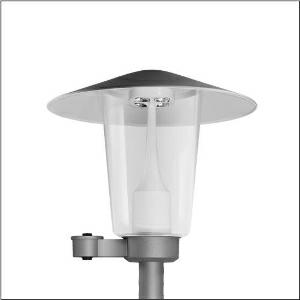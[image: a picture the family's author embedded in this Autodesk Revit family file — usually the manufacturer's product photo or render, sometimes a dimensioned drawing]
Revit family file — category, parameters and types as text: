
# Revit family: pilzleuchte_iq___st1_2a_5xa5235eu14h000022_6897
name_source: partatom
category: Lighting Fixtures
units: mm (PartAtom-declared; Revit-internal decimal feet)

## family parameters
Cut with Voids When Loaded = No
Host = Face
Light Source = No
Part Type = Normal
Room Calculation Point = No
Round Connector Dimension = Use Diameter
Shared = No

## types (1)
- --- (1 x LED, 1550 lm, 10.7 W, 3000K)
    Apparent Load = 11 VA
    CIE Flux Codes = 24 61 93 98 100
    Color Rendering = 70
    Color Temperature = 3000K
    Default Elevation = 1800 mm
    Description = Mushroom Luminaire iQ, mast luminaire, Module 540 iQ-SR, primary light control with 3 zone facetted reflector, of plastic, silver coated, highly specular, structured, primary optical cover: cover, of PMMA, transparent, light distribution: ST1.2a, light emission: direct distribution, primary light characteristic: asymmetric, installation type: post-top, LED, High Power LED, rated luminous flux: 1.550lm, luminous efficacy: 145lm/W, light colour: 730, colour temperature: 3000K, control gear: iQ-Street Remote, D4i with power reduction, control: optimised constant luminous flux control (CLO 2.0), Desk-Remote (wireless, voltage-free reading and setting of iQ features in the workshop via application-optimized NFC function/RFID function), Light-Fading, Smart-Wire, Night-Set, Lumen-Switch, Temp-Guard, Auto-Match, Street-Remote, pre-setting: logarithmic dimming characteristic, with terminal, 6-pole, max. 2.5mm², mains connection: 230..240V, AC, 50/60Hz, connection cable pre-assembled, cable length: 5,5m, wiring characteristics: H07RN-F, start of lifetime: 11W, end of service life: 11W, reduction: 6W, luminaire housing, upper part, of glass-fibre reinforced polyester, coated, Siteco® metallic grey (DB 702S), diameter: 650mm, height: 586mm, spigot size: d x l = 76 x 70mm (post-top) | with reducer (optional accessory) 60 x 70mm, mounting height: 3..5m, post-top mast mounting element, of diecast aluminium, coated, Siteco® metallic grey (DB 702S), Module 540 iQ-SR, traffic white (RAL 9016), equipment: standard, Smart Interface below, protection rating (complete): IP65, insulation class (complete): insulation class II (safety insulation), certification: CE, ENEC, VDE, packaging unit: 1 piece

Light Distribution: ST1.2a
    Height = 586 mm
    Lamp = 1 x LED
    Lamp Light Flux = 1550 lm
    Lamp Power = 10.7 W
    Lamp count = 1
    Length = 650 mm
    Luminous efficacy = 145 lm/W
    Manufacturer = Siteco
    ModVariant = No
    Model = 5XA5235EU14H000022
    Number of Poles = 1
    OnlyDefault = Yes
    Power Factor = 1
    Product Name = Pilzleuchte iQ | ST1.2a
    Product group = mast luminaire | pylon top
    ProductGroupID = 6100
    Protection Class = Protection class II
    Protection Degree = IP 65
    RLX_Detail_Level = 1
    RLX_Emergency_Light_Flux = 0 lm
    RLX_Emergency_Type = 0
    RLX_Emergency_Type_DB = No
    RlxData = <blob elided: 51765 chars, md5=b7cebe9e>
    Socket = socket
    Standby Power = 0 W
    System Light Flux = 1550 lm
    System Power = 11 W
    Type Comments = factory setting: luminous flux: 100 % | dim-lin: 254 | 419 mA
    Type Image = l_1006957.jpg
    URL = http://relux.com
    VarID = @adj_086856
    Voltage = 0 V
    Weight = 0.00 kg
    Width = 0 mm  [stored 0 ft]

note: [stored X ft] marks values corroborated as IEEE doubles in the binary element streams (Revit-internal decimal feet)

## geometry (parser evidence)
native form markers: Blend x4, Sweep x9
no freeform markers — native parametric forms only
